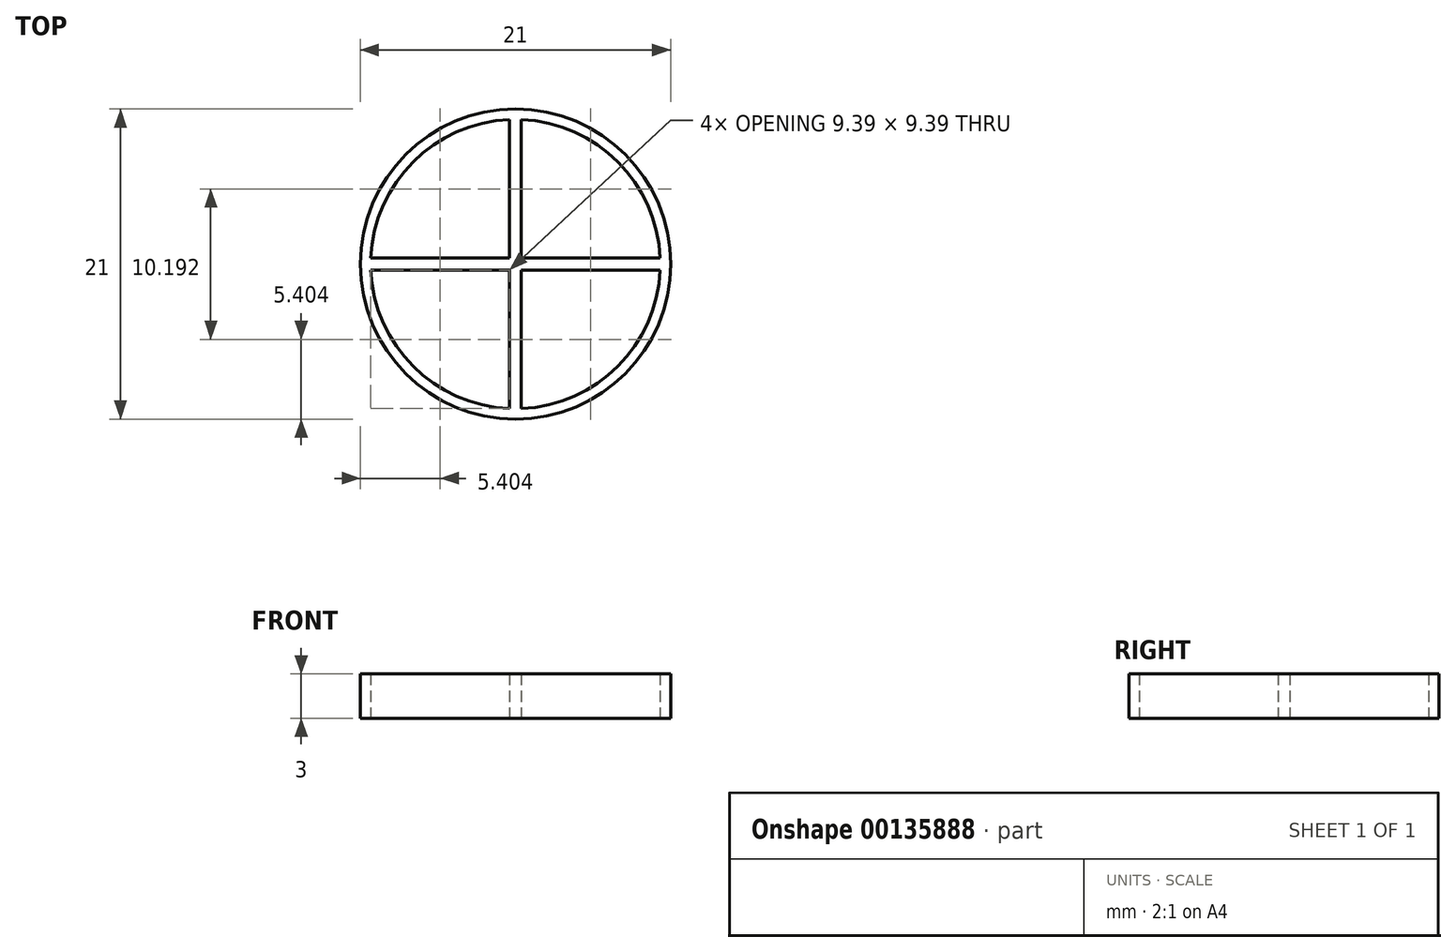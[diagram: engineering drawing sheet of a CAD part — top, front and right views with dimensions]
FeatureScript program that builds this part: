
annotation { "Feature Type Name" : "Feature", "Feature Type Description" : "" }
export const myFeature = defineFeature(function(context is Context, id is Id, definition is map)
    precondition{}
    {
        {
            var Q0;
            Q0=qCreatedBy(makeId("Top.planeOp"),FACE);
            var sketch = newSketch(context, id + "F0", { "sketchPlane" : qUnion([Q0])});
            skCircle(sketch, "E0", {"center": v(0, 0) * mm, "radius": 10.5 * mm});
            skArc(sketch, "E1", {"start": v(-0.4, -9.8) * mm, "mid": v(-6.93, -6.93) * mm, "end": v(-9.8, -0.4) * mm});
            skArc(sketch, "E2", {"start": v(9.8, -0.4) * mm, "mid": v(6.93, -6.93) * mm, "end": v(0.4, -9.8) * mm});
            skArc(sketch, "E3", {"start": v(0.4, 9.8) * mm, "mid": v(6.93, 6.93) * mm, "end": v(9.8, 0.4) * mm});
            skArc(sketch, "E4", {"start": v(-0.4, 9.8) * mm, "mid": v(-6.93, 6.93) * mm, "end": v(-9.8, 0.4) * mm});
            skLineSegment(sketch, "E5", {"start": v(-9.8, 0.4) * mm, "end": v(-0.4, 0.4) * mm});
            skLineSegment(sketch, "E6", {"start": v(-9.8, -0.4) * mm, "end": v(-0.4, -0.4) * mm});
            skLineSegment(sketch, "E7", {"start": v(-0.4, -0.4) * mm, "end": v(-0.4, -9.8) * mm});
            skLineSegment(sketch, "E8", {"start": v(9.8, -0.4) * mm, "end": v(0.4, -0.4) * mm});
            skLineSegment(sketch, "E9", {"start": v(0.4, -0.4) * mm, "end": v(0.4, -9.8) * mm});
            skLineSegment(sketch, "E10", {"start": v(9.8, 0.4) * mm, "end": v(0.4, 0.4) * mm});
            skLineSegment(sketch, "E11", {"start": v(0.4, 0.4) * mm, "end": v(0.4, 9.8) * mm});
            skLineSegment(sketch, "E12", {"start": v(-0.4, 9.8) * mm, "end": v(-0.4, 0.4) * mm});
            skSolve(sketch);
        }
        {
            var Q0;
            Q0 = qSketchRegion(id + "F0", true);
            extrude(context, id + "F1", {"entities" : qUnion([Q0]), "depth" : 3 * mm});
        }
    });
